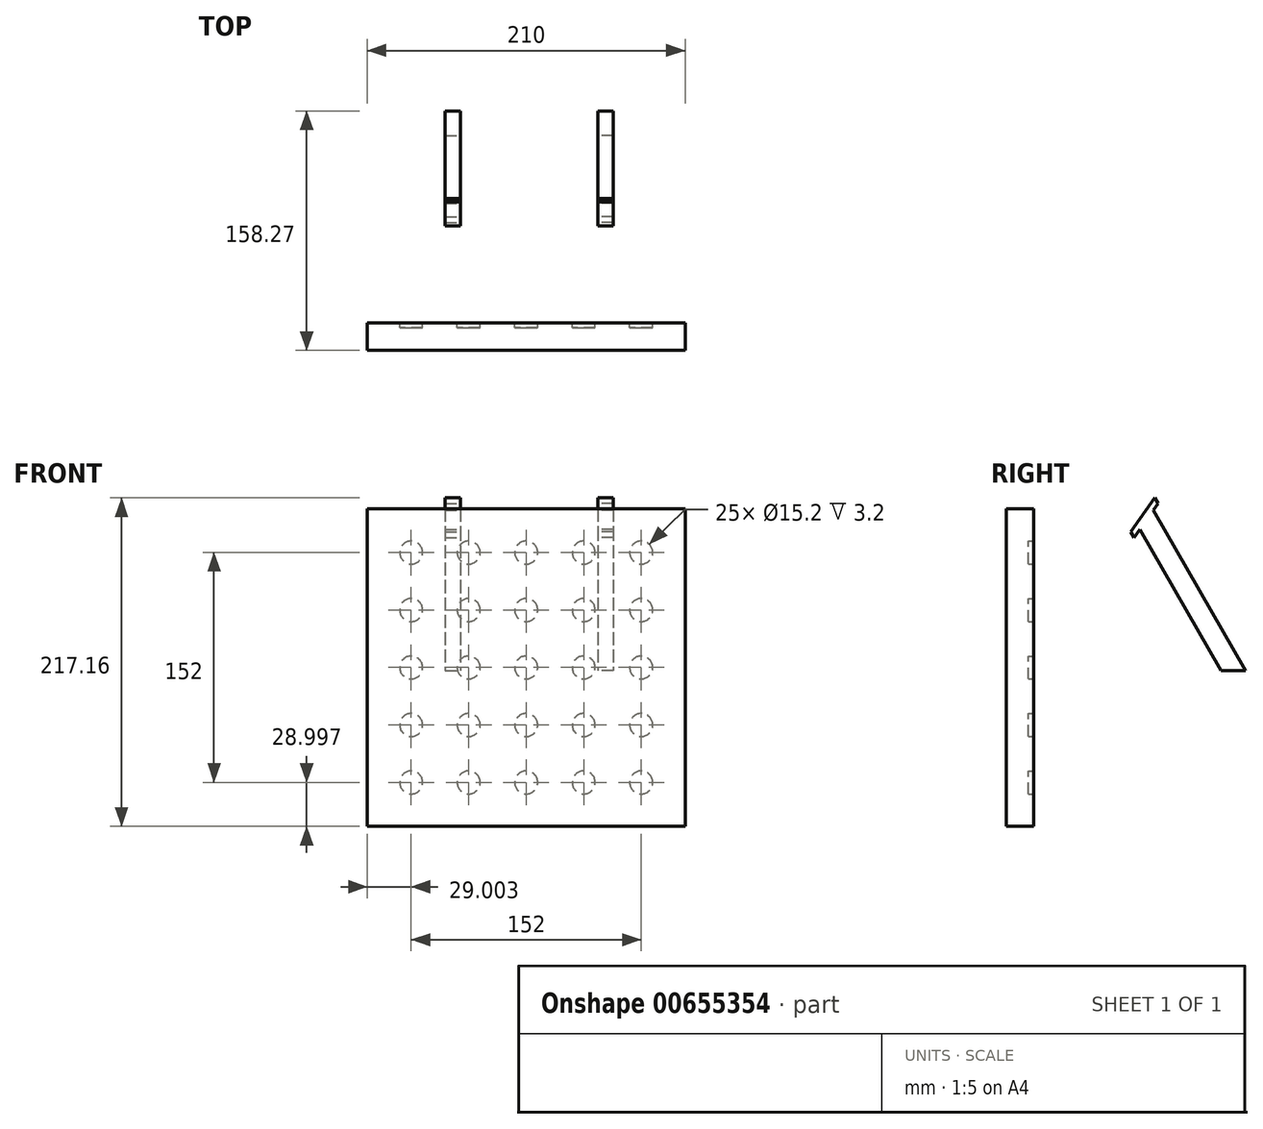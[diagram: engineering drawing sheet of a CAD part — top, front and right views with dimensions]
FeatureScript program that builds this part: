
annotation { "Feature Type Name" : "Feature", "Feature Type Description" : "" }
export const myFeature = defineFeature(function(context is Context, id is Id, definition is map)
    precondition{}
    {
        {
            var Q0;
            Q0=qCreatedBy(makeId("Front.planeOp"),FACE);
            var sketch = newSketch(context, id + "F0", { "sketchPlane" : qUnion([Q0])});
            skLineSegment(sketch, "E0.bottom", {"start": v(-106.96, 107.16) * mm, "end": v(103.04, 107.16) * mm});
            skLineSegment(sketch, "E0.top", {"start": v(-106.96, -102.84) * mm, "end": v(103.04, -102.84) * mm});
            skLineSegment(sketch, "E0.left", {"start": v(-106.96, 107.16) * mm, "end": v(-106.96, -102.84) * mm});
            skLineSegment(sketch, "E0.right", {"start": v(103.04, 107.16) * mm, "end": v(103.04, -102.84) * mm});
            skCircle(sketch, "E1", {"center": v(-77.96, 78.16) * mm, "radius": 7.6 * mm});
            skCircle(sketch, "E2.0.1.0", {"center": v(-77.96, 40.16) * mm, "radius": 7.6 * mm});
            skCircle(sketch, "E2.0.2.0", {"center": v(-77.96, 2.16) * mm, "radius": 7.6 * mm});
            skCircle(sketch, "E2.0.3.0", {"center": v(-77.96, -35.84) * mm, "radius": 7.6 * mm});
            skCircle(sketch, "E2.0.4.0", {"center": v(-77.96, -73.84) * mm, "radius": 7.6 * mm});
            skCircle(sketch, "E2.1.0.0", {"center": v(-39.96, 78.16) * mm, "radius": 7.6 * mm});
            skCircle(sketch, "E2.1.1.0", {"center": v(-39.96, 40.16) * mm, "radius": 7.6 * mm});
            skCircle(sketch, "E2.1.2.0", {"center": v(-39.96, 2.16) * mm, "radius": 7.6 * mm});
            skCircle(sketch, "E2.1.3.0", {"center": v(-39.96, -35.84) * mm, "radius": 7.6 * mm});
            skCircle(sketch, "E2.1.4.0", {"center": v(-39.96, -73.84) * mm, "radius": 7.6 * mm});
            skCircle(sketch, "E2.2.0.0", {"center": v(-1.96, 78.16) * mm, "radius": 7.6 * mm});
            skCircle(sketch, "E2.2.1.0", {"center": v(-1.96, 40.16) * mm, "radius": 7.6 * mm});
            skCircle(sketch, "E2.2.2.0", {"center": v(-1.96, 2.16) * mm, "radius": 7.6 * mm});
            skCircle(sketch, "E2.2.3.0", {"center": v(-1.96, -35.84) * mm, "radius": 7.6 * mm});
            skCircle(sketch, "E2.2.4.0", {"center": v(-1.96, -73.84) * mm, "radius": 7.6 * mm});
            skCircle(sketch, "E2.3.0.0", {"center": v(36.04, 78.16) * mm, "radius": 7.6 * mm});
            skCircle(sketch, "E2.3.1.0", {"center": v(36.04, 40.16) * mm, "radius": 7.6 * mm});
            skCircle(sketch, "E2.3.2.0", {"center": v(36.04, 2.16) * mm, "radius": 7.6 * mm});
            skCircle(sketch, "E2.3.3.0", {"center": v(36.04, -35.84) * mm, "radius": 7.6 * mm});
            skCircle(sketch, "E2.3.4.0", {"center": v(36.04, -73.84) * mm, "radius": 7.6 * mm});
            skCircle(sketch, "E2.4.0.0", {"center": v(74.04, 78.16) * mm, "radius": 7.6 * mm});
            skCircle(sketch, "E2.4.1.0", {"center": v(74.04, 40.16) * mm, "radius": 7.6 * mm});
            skCircle(sketch, "E2.4.2.0", {"center": v(74.04, 2.16) * mm, "radius": 7.6 * mm});
            skCircle(sketch, "E2.4.3.0", {"center": v(74.04, -35.84) * mm, "radius": 7.6 * mm});
            skCircle(sketch, "E2.4.4.0", {"center": v(74.04, -73.84) * mm, "radius": 7.6 * mm});
            skLineSegment(sketch, "E2.direction1", {"start": v(-77.96, 78.16) * mm, "end": v(-39.96, 78.16) * mm, "construction": true});
            skLineSegment(sketch, "E2.direction2", {"start": v(-77.96, 78.16) * mm, "end": v(-77.96, 40.16) * mm, "construction": true});
            skSolve(sketch);
        }
        {
            var Q0;
            Q0=makeQuery(id+"F0.imprint","IMPRINT",FACE,{"disambiguationData":[TD([[makeQuery(id+"F0.imprint","IMPRINT",EDGE,{"derivedFrom":sQuery(id+"F0.wireOp",EDGE,"E0.bottom")}),-1.0]])]});
            var Q1;
            Q1=makeQuery(id+"F0.imprint","IMPRINT",FACE,{"disambiguationData":[TD([[makeQuery(id+"F0.imprint","IMPRINT",EDGE,{"derivedFrom":sQuery(id+"F0.wireOp",EDGE,"E1")}),1.0]])]});
            var Q2;
            Q2=makeQuery(id+"F0.imprint","IMPRINT",FACE,{"disambiguationData":[TD([[makeQuery(id+"F0.imprint","IMPRINT",EDGE,{"derivedFrom":sQuery(id+"F0.wireOp",EDGE,"E2.0.1.0")}),1.0]])]});
            var Q3;
            Q3=makeQuery(id+"F0.imprint","IMPRINT",FACE,{"disambiguationData":[TD([[makeQuery(id+"F0.imprint","IMPRINT",EDGE,{"derivedFrom":sQuery(id+"F0.wireOp",EDGE,"E2.0.2.0")}),1.0]])]});
            var Q4;
            Q4=makeQuery(id+"F0.imprint","IMPRINT",FACE,{"disambiguationData":[TD([[makeQuery(id+"F0.imprint","IMPRINT",EDGE,{"derivedFrom":sQuery(id+"F0.wireOp",EDGE,"E2.0.3.0")}),1.0]])]});
            var Q5;
            Q5=makeQuery(id+"F0.imprint","IMPRINT",FACE,{"disambiguationData":[TD([[makeQuery(id+"F0.imprint","IMPRINT",EDGE,{"derivedFrom":sQuery(id+"F0.wireOp",EDGE,"E2.0.4.0")}),1.0]])]});
            var Q6;
            Q6=makeQuery(id+"F0.imprint","IMPRINT",FACE,{"disambiguationData":[TD([[makeQuery(id+"F0.imprint","IMPRINT",EDGE,{"derivedFrom":sQuery(id+"F0.wireOp",EDGE,"E2.1.4.0")}),1.0]])]});
            var Q7;
            Q7=makeQuery(id+"F0.imprint","IMPRINT",FACE,{"disambiguationData":[TD([[makeQuery(id+"F0.imprint","IMPRINT",EDGE,{"derivedFrom":sQuery(id+"F0.wireOp",EDGE,"E2.1.3.0")}),1.0]])]});
            var Q8;
            Q8=makeQuery(id+"F0.imprint","IMPRINT",FACE,{"disambiguationData":[TD([[makeQuery(id+"F0.imprint","IMPRINT",EDGE,{"derivedFrom":sQuery(id+"F0.wireOp",EDGE,"E2.1.2.0")}),1.0]])]});
            var Q9;
            Q9=makeQuery(id+"F0.imprint","IMPRINT",FACE,{"disambiguationData":[TD([[makeQuery(id+"F0.imprint","IMPRINT",EDGE,{"derivedFrom":sQuery(id+"F0.wireOp",EDGE,"E2.2.2.0")}),1.0]])]});
            var Q10;
            Q10=makeQuery(id+"F0.imprint","IMPRINT",FACE,{"disambiguationData":[TD([[makeQuery(id+"F0.imprint","IMPRINT",EDGE,{"derivedFrom":sQuery(id+"F0.wireOp",EDGE,"E2.2.1.0")}),1.0]])]});
            var Q11;
            Q11=makeQuery(id+"F0.imprint","IMPRINT",FACE,{"disambiguationData":[TD([[makeQuery(id+"F0.imprint","IMPRINT",EDGE,{"derivedFrom":sQuery(id+"F0.wireOp",EDGE,"E2.2.0.0")}),1.0]])]});
            var Q12;
            Q12=makeQuery(id+"F0.imprint","IMPRINT",FACE,{"disambiguationData":[TD([[makeQuery(id+"F0.imprint","IMPRINT",EDGE,{"derivedFrom":sQuery(id+"F0.wireOp",EDGE,"E2.3.0.0")}),1.0]])]});
            var Q13;
            Q13=makeQuery(id+"F0.imprint","IMPRINT",FACE,{"disambiguationData":[TD([[makeQuery(id+"F0.imprint","IMPRINT",EDGE,{"derivedFrom":sQuery(id+"F0.wireOp",EDGE,"E2.3.1.0")}),1.0]])]});
            var Q14;
            Q14=makeQuery(id+"F0.imprint","IMPRINT",FACE,{"disambiguationData":[TD([[makeQuery(id+"F0.imprint","IMPRINT",EDGE,{"derivedFrom":sQuery(id+"F0.wireOp",EDGE,"E2.3.2.0")}),1.0]])]});
            var Q15;
            Q15=makeQuery(id+"F0.imprint","IMPRINT",FACE,{"disambiguationData":[TD([[makeQuery(id+"F0.imprint","IMPRINT",EDGE,{"derivedFrom":sQuery(id+"F0.wireOp",EDGE,"E2.3.3.0")}),1.0]])]});
            var Q16;
            Q16=makeQuery(id+"F0.imprint","IMPRINT",FACE,{"disambiguationData":[TD([[makeQuery(id+"F0.imprint","IMPRINT",EDGE,{"derivedFrom":sQuery(id+"F0.wireOp",EDGE,"E2.3.4.0")}),1.0]])]});
            var Q17;
            Q17=makeQuery(id+"F0.imprint","IMPRINT",FACE,{"disambiguationData":[TD([[makeQuery(id+"F0.imprint","IMPRINT",EDGE,{"derivedFrom":sQuery(id+"F0.wireOp",EDGE,"E2.4.4.0")}),1.0]])]});
            var Q18;
            Q18=makeQuery(id+"F0.imprint","IMPRINT",FACE,{"disambiguationData":[TD([[makeQuery(id+"F0.imprint","IMPRINT",EDGE,{"derivedFrom":sQuery(id+"F0.wireOp",EDGE,"E2.4.3.0")}),1.0]])]});
            var Q19;
            Q19=makeQuery(id+"F0.imprint","IMPRINT",FACE,{"disambiguationData":[TD([[makeQuery(id+"F0.imprint","IMPRINT",EDGE,{"derivedFrom":sQuery(id+"F0.wireOp",EDGE,"E2.4.1.0")}),1.0]])]});
            var Q20;
            Q20=makeQuery(id+"F0.imprint","IMPRINT",FACE,{"disambiguationData":[TD([[makeQuery(id+"F0.imprint","IMPRINT",EDGE,{"derivedFrom":sQuery(id+"F0.wireOp",EDGE,"E2.4.0.0")}),1.0]])]});
            var Q21;
            Q21=makeQuery(id+"F0.imprint","IMPRINT",FACE,{"disambiguationData":[TD([[makeQuery(id+"F0.imprint","IMPRINT",EDGE,{"derivedFrom":sQuery(id+"F0.wireOp",EDGE,"E2.1.0.0")}),1.0]])]});
            var Q22;
            Q22=makeQuery(id+"F0.imprint","IMPRINT",FACE,{"disambiguationData":[TD([[makeQuery(id+"F0.imprint","IMPRINT",EDGE,{"derivedFrom":sQuery(id+"F0.wireOp",EDGE,"E2.2.3.0")}),1.0]])]});
            var Q23;
            Q23=makeQuery(id+"F0.imprint","IMPRINT",FACE,{"disambiguationData":[TD([[makeQuery(id+"F0.imprint","IMPRINT",EDGE,{"derivedFrom":sQuery(id+"F0.wireOp",EDGE,"E2.2.4.0")}),1.0]])]});
            var Q24;
            Q24=makeQuery(id+"F0.imprint","IMPRINT",FACE,{"disambiguationData":[TD([[makeQuery(id+"F0.imprint","IMPRINT",EDGE,{"derivedFrom":sQuery(id+"F0.wireOp",EDGE,"E2.4.2.0")}),1.0]])]});
            var Q25;
            Q25=makeQuery(id+"F0.imprint","IMPRINT",FACE,{"disambiguationData":[TD([[makeQuery(id+"F0.imprint","IMPRINT",EDGE,{"derivedFrom":sQuery(id+"F0.wireOp",EDGE,"E2.1.1.0")}),1.0]])]});
            extrude(context, id + "F1", {"entities" : qUnion([Q0, Q1, Q2, Q3, Q4, Q5, Q6, Q7, Q8, Q9, Q10, Q11, Q12, Q13, Q14, Q15, Q16, Q17, Q18, Q19, Q20, Q21, Q22, Q23, Q24, Q25]), "depth" : 18 * mm, "offsetDistance" : 25 * mm});
        }
        {
            var Q0;
            Q0=makeQuery(id+"F0.imprint","IMPRINT",FACE,{"disambiguationData":[TD([[makeQuery(id+"F0.imprint","IMPRINT",EDGE,{"derivedFrom":sQuery(id+"F0.wireOp",EDGE,"E2.4.0.0")}),1.0]])]});
            var Q1;
            Q1=makeQuery(id+"F0.imprint","IMPRINT",FACE,{"disambiguationData":[TD([[makeQuery(id+"F0.imprint","IMPRINT",EDGE,{"derivedFrom":sQuery(id+"F0.wireOp",EDGE,"E2.3.0.0")}),1.0]])]});
            var Q2;
            Q2=makeQuery(id+"F0.imprint","IMPRINT",FACE,{"disambiguationData":[TD([[makeQuery(id+"F0.imprint","IMPRINT",EDGE,{"derivedFrom":sQuery(id+"F0.wireOp",EDGE,"E2.3.1.0")}),1.0]])]});
            var Q3;
            Q3=makeQuery(id+"F0.imprint","IMPRINT",FACE,{"disambiguationData":[TD([[makeQuery(id+"F0.imprint","IMPRINT",EDGE,{"derivedFrom":sQuery(id+"F0.wireOp",EDGE,"E2.4.1.0")}),1.0]])]});
            var Q4;
            Q4=makeQuery(id+"F0.imprint","IMPRINT",FACE,{"disambiguationData":[TD([[makeQuery(id+"F0.imprint","IMPRINT",EDGE,{"derivedFrom":sQuery(id+"F0.wireOp",EDGE,"E2.4.2.0")}),1.0]])]});
            var Q5;
            Q5=makeQuery(id+"F0.imprint","IMPRINT",FACE,{"disambiguationData":[TD([[makeQuery(id+"F0.imprint","IMPRINT",EDGE,{"derivedFrom":sQuery(id+"F0.wireOp",EDGE,"E2.4.3.0")}),1.0]])]});
            var Q6;
            Q6=makeQuery(id+"F0.imprint","IMPRINT",FACE,{"disambiguationData":[TD([[makeQuery(id+"F0.imprint","IMPRINT",EDGE,{"derivedFrom":sQuery(id+"F0.wireOp",EDGE,"E2.3.3.0")}),1.0]])]});
            var Q7;
            Q7=makeQuery(id+"F0.imprint","IMPRINT",FACE,{"disambiguationData":[TD([[makeQuery(id+"F0.imprint","IMPRINT",EDGE,{"derivedFrom":sQuery(id+"F0.wireOp",EDGE,"E2.3.2.0")}),1.0]])]});
            var Q8;
            Q8=makeQuery(id+"F0.imprint","IMPRINT",FACE,{"disambiguationData":[TD([[makeQuery(id+"F0.imprint","IMPRINT",EDGE,{"derivedFrom":sQuery(id+"F0.wireOp",EDGE,"E2.4.4.0")}),1.0]])]});
            var Q9;
            Q9=makeQuery(id+"F0.imprint","IMPRINT",FACE,{"disambiguationData":[TD([[makeQuery(id+"F0.imprint","IMPRINT",EDGE,{"derivedFrom":sQuery(id+"F0.wireOp",EDGE,"E2.3.4.0")}),1.0]])]});
            var Q10;
            Q10=makeQuery(id+"F0.imprint","IMPRINT",FACE,{"disambiguationData":[TD([[makeQuery(id+"F0.imprint","IMPRINT",EDGE,{"derivedFrom":sQuery(id+"F0.wireOp",EDGE,"E2.2.4.0")}),1.0]])]});
            var Q11;
            Q11=makeQuery(id+"F0.imprint","IMPRINT",FACE,{"disambiguationData":[TD([[makeQuery(id+"F0.imprint","IMPRINT",EDGE,{"derivedFrom":sQuery(id+"F0.wireOp",EDGE,"E2.2.3.0")}),1.0]])]});
            var Q12;
            Q12=makeQuery(id+"F0.imprint","IMPRINT",FACE,{"disambiguationData":[TD([[makeQuery(id+"F0.imprint","IMPRINT",EDGE,{"derivedFrom":sQuery(id+"F0.wireOp",EDGE,"E2.2.2.0")}),1.0]])]});
            var Q13;
            Q13=makeQuery(id+"F0.imprint","IMPRINT",FACE,{"disambiguationData":[TD([[makeQuery(id+"F0.imprint","IMPRINT",EDGE,{"derivedFrom":sQuery(id+"F0.wireOp",EDGE,"E2.2.1.0")}),1.0]])]});
            var Q14;
            Q14=makeQuery(id+"F0.imprint","IMPRINT",FACE,{"disambiguationData":[TD([[makeQuery(id+"F0.imprint","IMPRINT",EDGE,{"derivedFrom":sQuery(id+"F0.wireOp",EDGE,"E2.1.0.0")}),1.0]])]});
            var Q15;
            Q15=makeQuery(id+"F0.imprint","IMPRINT",FACE,{"disambiguationData":[TD([[makeQuery(id+"F0.imprint","IMPRINT",EDGE,{"derivedFrom":sQuery(id+"F0.wireOp",EDGE,"E2.2.0.0")}),1.0]])]});
            var Q16;
            Q16=makeQuery(id+"F0.imprint","IMPRINT",FACE,{"disambiguationData":[TD([[makeQuery(id+"F0.imprint","IMPRINT",EDGE,{"derivedFrom":sQuery(id+"F0.wireOp",EDGE,"E2.1.1.0")}),1.0]])]});
            var Q17;
            Q17=makeQuery(id+"F0.imprint","IMPRINT",FACE,{"disambiguationData":[TD([[makeQuery(id+"F0.imprint","IMPRINT",EDGE,{"derivedFrom":sQuery(id+"F0.wireOp",EDGE,"E2.1.2.0")}),1.0]])]});
            var Q18;
            Q18=makeQuery(id+"F0.imprint","IMPRINT",FACE,{"disambiguationData":[TD([[makeQuery(id+"F0.imprint","IMPRINT",EDGE,{"derivedFrom":sQuery(id+"F0.wireOp",EDGE,"E2.1.3.0")}),1.0]])]});
            var Q19;
            Q19=makeQuery(id+"F0.imprint","IMPRINT",FACE,{"disambiguationData":[TD([[makeQuery(id+"F0.imprint","IMPRINT",EDGE,{"derivedFrom":sQuery(id+"F0.wireOp",EDGE,"E2.1.4.0")}),1.0]])]});
            var Q20;
            Q20=makeQuery(id+"F0.imprint","IMPRINT",FACE,{"disambiguationData":[TD([[makeQuery(id+"F0.imprint","IMPRINT",EDGE,{"derivedFrom":sQuery(id+"F0.wireOp",EDGE,"E2.0.4.0")}),1.0]])]});
            var Q21;
            Q21=makeQuery(id+"F0.imprint","IMPRINT",FACE,{"disambiguationData":[TD([[makeQuery(id+"F0.imprint","IMPRINT",EDGE,{"derivedFrom":sQuery(id+"F0.wireOp",EDGE,"E2.0.3.0")}),1.0]])]});
            var Q22;
            Q22=makeQuery(id+"F0.imprint","IMPRINT",FACE,{"disambiguationData":[TD([[makeQuery(id+"F0.imprint","IMPRINT",EDGE,{"derivedFrom":sQuery(id+"F0.wireOp",EDGE,"E2.0.2.0")}),1.0]])]});
            var Q23;
            Q23=makeQuery(id+"F0.imprint","IMPRINT",FACE,{"disambiguationData":[TD([[makeQuery(id+"F0.imprint","IMPRINT",EDGE,{"derivedFrom":sQuery(id+"F0.wireOp",EDGE,"E2.0.1.0")}),1.0]])]});
            var Q24;
            Q24=makeQuery(id+"F0.imprint","IMPRINT",FACE,{"disambiguationData":[TD([[makeQuery(id+"F0.imprint","IMPRINT",EDGE,{"derivedFrom":sQuery(id+"F0.wireOp",EDGE,"E1")}),1.0]])]});
            extrude(context, id + "F2", {"entities" : qUnion([Q0, Q1, Q2, Q3, Q4, Q5, Q6, Q7, Q8, Q9, Q10, Q11, Q12, Q13, Q14, Q15, Q16, Q17, Q18, Q19, Q20, Q21, Q22, Q23, Q24]), "operationType" : NewBodyOperationType.REMOVE, "depth" : 3.2 * mm, "offsetDistance" : 25 * mm});
        }
        {
            var Q0;
            Q0=qCreatedBy(makeId("Right.planeOp"),FACE);
            var sketch = newSketch(context, id + "F3", { "sketchPlane" : qUnion([Q0])});
            skLineSegment(sketch, "E3.bottom", {"start": v(64.22, 91.72) * mm, "end": v(85.87, 104.22) * mm, "construction": true});
            skLineSegment(sketch, "E3.top", {"start": v(117.18, 0) * mm, "end": v(138.83, 12.5) * mm, "construction": true});
            skLineSegment(sketch, "E3.left", {"start": v(64.22, 91.72) * mm, "end": v(117.18, 0) * mm});
            skLineSegment(sketch, "E3.right", {"start": v(85.87, 104.22) * mm, "end": v(138.83, 12.5) * mm});
            skLineSegment(sketch, "E4", {"start": v(85.87, 104.22) * mm, "end": v(80.04, 114.32) * mm});
            skLineSegment(sketch, "E5", {"start": v(80.04, 114.32) * mm, "end": v(64.22, 91.72) * mm});
            skLineSegment(sketch, "E6", {"start": v(138.83, 12.5) * mm, "end": v(146.04, 0) * mm});
            skLineSegment(sketch, "E7", {"start": v(146.04, 0) * mm, "end": v(117.18, 0) * mm});
            skLineSegment(sketch, "E8", {"start": v(0, 0) * mm, "end": v(96.65, 138.04) * mm, "construction": true});
            skPoint(sketch, "E9", {"position": v(72.13, 103.02) * mm});
            skLineSegment(sketch, "E10", {"start": v(82.25, 110.5) * mm, "end": v(66.43, 87.9) * mm});
            skLineSegment(sketch, "E11", {"start": v(143.16, 5) * mm, "end": v(114.3, 5) * mm});
            skLineSegment(sketch, "E12", {"start": v(79.09, 105.97) * mm, "end": v(137.38, 5) * mm});
            skLineSegment(sketch, "E13", {"start": v(137.38, 5) * mm, "end": v(140.27, 0) * mm});
            skLineSegment(sketch, "E14", {"start": v(70.23, 93.32) * mm, "end": v(124.1, 0) * mm});
            skSolve(sketch);
        }
        {
            var Q0;
            {var subQ4=sQuery(id+"F3.wireOp",EDGE,"E5");Q0=makeQuery(id+"F3.imprint","IMPRINT",FACE,{"disambiguationData":[TD([[makeQuery(id+"F3.imprint","IMPRINT",EDGE,{"derivedFrom":subQ4}),1.0]])]});}
            var Q1;
            {var subQ0=sQuery(id+"F3.wireOp",EDGE,"E13");Q1=makeQuery(id+"F3.imprint","IMPRINT",FACE,{"disambiguationData":[TD([[makeQuery(id+"F3.imprint","IMPRINT",EDGE,{"derivedFrom":subQ0}),-1.0]])]});}
            var Q2;
            {var subQ0=sQuery(id+"F3.wireOp",EDGE,"E12");Q2=makeQuery(id+"F3.imprint","IMPRINT",FACE,{"disambiguationData":[TD([[makeQuery(id+"F3.imprint","IMPRINT",EDGE,{"derivedFrom":subQ0}),-1.0]])]});}
            extrude(context, id + "F4", {"entities" : qUnion([Q0, Q1, Q2]), "depth" : 55.5 * mm, "offsetDistance" : 25 * mm, "hasSecondDirection" : true, "secondDirectionOppositeDirection" : false, "secondDirectionDepth" : 45.5 * mm});
        }
        {
            var Q0;
            Q0=makeQuery(id+"F4.opExtrude","SWEPT_BODY",BODY,{"disambiguationData":[OSD([sQuery(id+"F3.wireOp",EDGE,"E3.left"),sQuery(id+"F3.wireOp",EDGE,"E3.right"),sQuery(id+"F3.wireOp",EDGE,"E4"),sQuery(id+"F3.wireOp",EDGE,"E5"),sQuery(id+"F3.wireOp",EDGE,"E6"),sQuery(id+"F3.wireOp",EDGE,"E7")])]});
            var Q1;
            Q1=qCreatedBy(makeId("Right.planeOp"),FACE);
            mirror(context, id + "F5", {"entities" : qUnion([Q0]), "mirrorPlane" : qUnion([Q1])});
        }
    });
